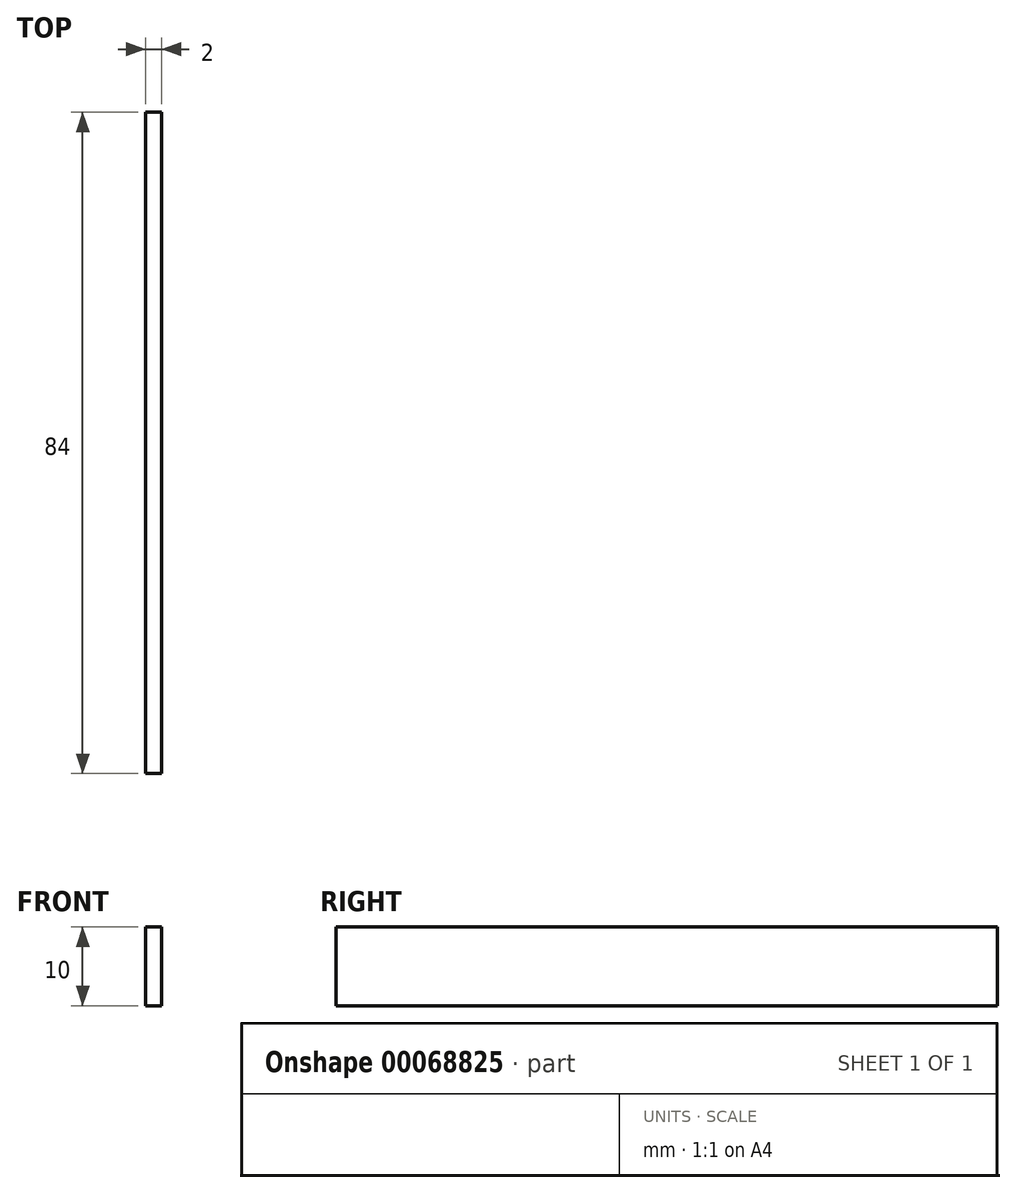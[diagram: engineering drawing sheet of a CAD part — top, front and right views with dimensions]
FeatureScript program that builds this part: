
annotation { "Feature Type Name" : "Feature", "Feature Type Description" : "" }
export const myFeature = defineFeature(function(context is Context, id is Id, definition is map)
    precondition{}
    {
        {
            var Q0;
            Q0=qCreatedBy(makeId("Right.planeOp"),FACE);
            var sketch = newSketch(context, id + "F0", { "sketchPlane" : qUnion([Q0])});
            skLineSegment(sketch, "E0.bottom", {"start": v(0, 0) * mm, "end": v(84, 0) * mm});
            skLineSegment(sketch, "E0.top", {"start": v(0, 10) * mm, "end": v(84, 10) * mm});
            skLineSegment(sketch, "E0.left", {"start": v(0, 0) * mm, "end": v(0, 10) * mm});
            skLineSegment(sketch, "E0.right", {"start": v(84, 0) * mm, "end": v(84, 10) * mm});
            skSolve(sketch);
        }
        {
            var Q0;
            Q0 = qSketchRegion(id + "F0", true);
            extrude(context, id + "F1", {"entities" : qUnion([Q0]), "depth" : 2 * mm});
        }
    });
